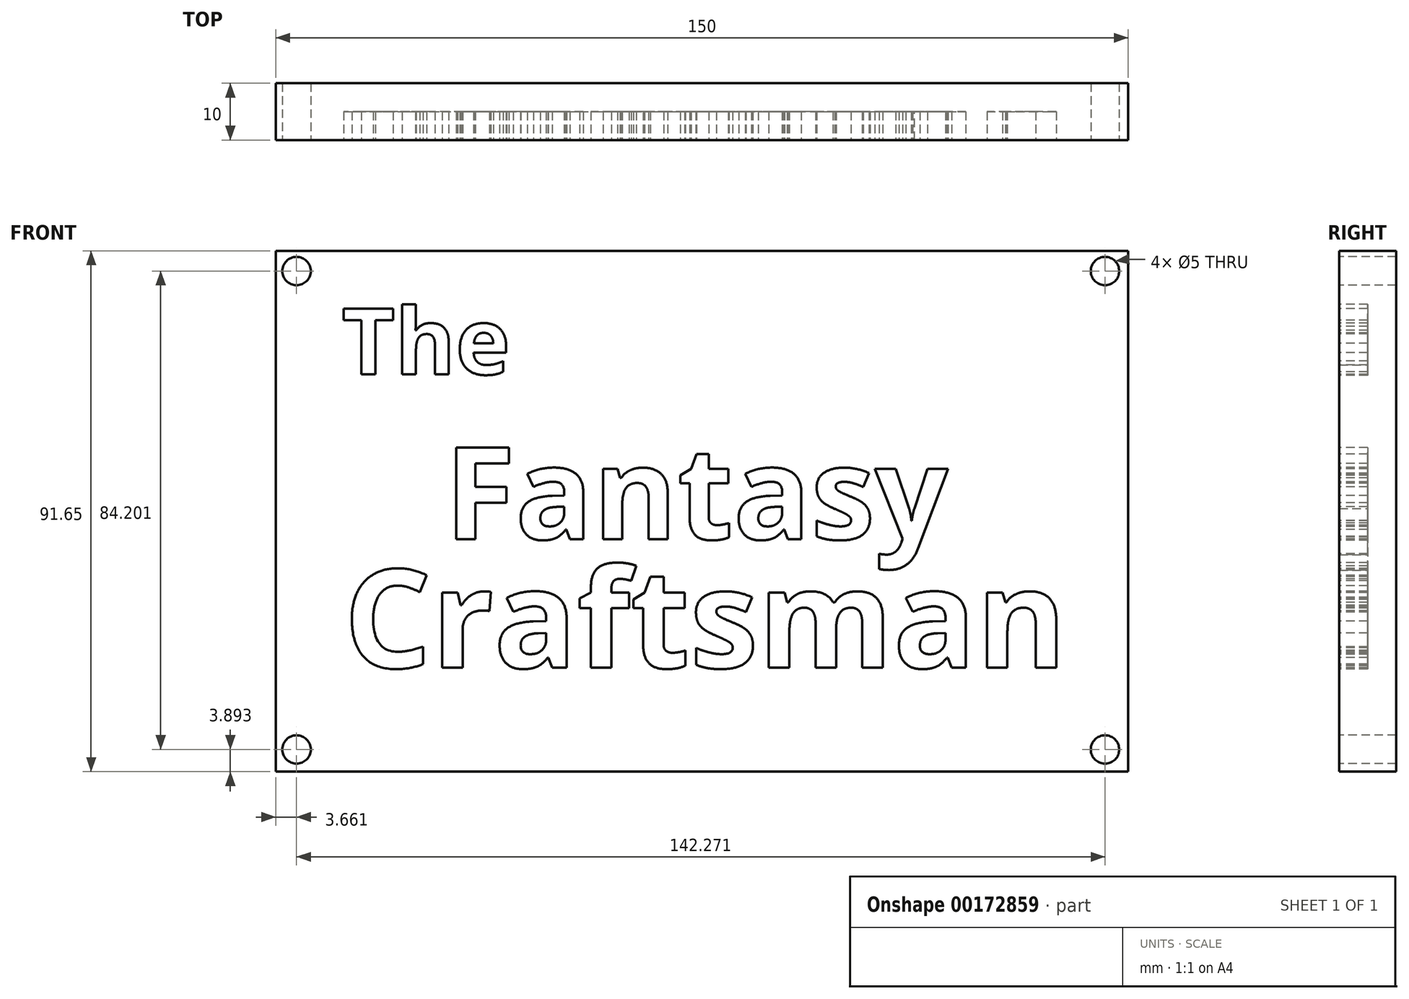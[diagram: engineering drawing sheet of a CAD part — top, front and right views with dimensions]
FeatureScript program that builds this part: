
annotation { "Feature Type Name" : "Feature", "Feature Type Description" : "" }
export const myFeature = defineFeature(function(context is Context, id is Id, definition is map)
    precondition{}
    {
        {
            var Q0;
            Q0=qCreatedBy(makeId("Front.planeOp"),FACE);
            var sketch = newSketch(context, id + "F0", { "sketchPlane" : qUnion([Q0])});
            skLineSegment(sketch, "E0.bottom", {"start": v(-73.96, 55.96) * mm, "end": v(76.04, 55.96) * mm});
            skLineSegment(sketch, "E0.top", {"start": v(-73.96, -35.7) * mm, "end": v(76.04, -35.7) * mm});
            skLineSegment(sketch, "E0.left", {"start": v(-73.96, 55.96) * mm, "end": v(-73.96, -35.7) * mm});
            skLineSegment(sketch, "E0.right", {"start": v(76.04, 55.96) * mm, "end": v(76.04, -35.7) * mm});
            skSolve(sketch);
        }
        {
            var Q0;
            Q0=makeQuery(id+"F0.imprint","IMPRINT",FACE,{"disambiguationData":[TD([[makeQuery(id+"F0.imprint","IMPRINT",EDGE,{"derivedFrom":sQuery(id+"F0.wireOp",EDGE,"E0.bottom")}),-1.0]])]});
            extrude(context, id + "F1", {"entities" : qUnion([Q0]), "depth" : 10 * mm});
        }
        {
            var Q0;
            Q0=makeQuery(id+"F1.opExtrude","CAP_FACE",FACE,{"disambiguationData":[OSD([sQuery(id+"F0.wireOp",EDGE,"E0.bottom"),sQuery(id+"F0.wireOp",EDGE,"E0.top"),sQuery(id+"F0.wireOp",EDGE,"E0.left"),sQuery(id+"F0.wireOp",EDGE,"E0.right")])],"isStart":false});
            var sketch = newSketch(context, id + "F2", { "sketchPlane" : qUnion([Q0])});
            skText(sketch, "E1", { "text": "The", "fontName": "OpenSans-Bold.ttf"});
            const initialGuessF2  = {"E1": [-0.06236, 0.03423, 1, 0, 0.01168]};
            skSetInitialGuess(sketch, initialGuessF2);
            skSolve(sketch);
        }
        {
            var Q0;
            Q0=makeQuery(id+"F2.imprint","IMPRINT",FACE,{"disambiguationData":[TD([[makeQuery(id+"F2.imprint","IMPRINT",EDGE,{"derivedFrom":sQuery(id+"F2.wireOp",EDGE,"E1.sketch_text.stroke-0")}),1.0]])]});
            var sketch = newSketch(context, id + "F3", { "sketchPlane" : qUnion([Q0])});
            skText(sketch, "E2", { "text": "Fantasy", "fontName": "OpenSans-Bold.ttf"});
            const initialGuessF3  = {"E2": [-0.04422, 0.00522, 1, 0, 0.01629]};
            skSetInitialGuess(sketch, initialGuessF3);
            skSolve(sketch);
        }
        {
            var Q0;
            Q0=makeQuery(id+"F2.imprint","IMPRINT",FACE,{"disambiguationData":[TD([[makeQuery(id+"F2.imprint","IMPRINT",EDGE,{"derivedFrom":sQuery(id+"F2.wireOp",EDGE,"E1.sketch_text.stroke-0")}),1.0]])]});
            var sketch = newSketch(context, id + "F4", { "sketchPlane" : qUnion([Q0])});
            skText(sketch, "E3", { "text": "Craftsman", "fontName": "OpenSans-Bold.ttf"});
            const initialGuessF4  = {"E3": [-0.06198, -0.01742, 1, 0, 0.01742]};
            skSetInitialGuess(sketch, initialGuessF4);
            skSolve(sketch);
        }
        {
            var Q0;
            Q0=makeQuery(id+"F2.imprint","IMPRINT",FACE,{"disambiguationData":[TD([[makeQuery(id+"F2.imprint","IMPRINT",EDGE,{"derivedFrom":sQuery(id+"F2.wireOp",EDGE,"E1.sketch_text.stroke-0")}),1.0]])]});
            var sketch = newSketch(context, id + "F5", { "sketchPlane" : qUnion([Q0])});
            skPoint(sketch, "E4", {"position": v(-70.3, 52.4) * mm});
            skPoint(sketch, "E5", {"position": v(-70.3, -31.8) * mm});
            skPoint(sketch, "E6", {"position": v(71.97, -31.8) * mm});
            skPoint(sketch, "E7", {"position": v(71.97, 52.4) * mm});
            skSolve(sketch);
        }
        {
            var Q0;
            Q0=sQuery(id+"F5.wireOp",VERTEX,"E4");
            var Q1;
            Q1=sQuery(id+"F5.wireOp",VERTEX,"E5");
            var Q2;
            Q2=sQuery(id+"F5.wireOp",VERTEX,"E7");
            var Q3;
            Q3=sQuery(id+"F5.wireOp",VERTEX,"E6");
            var Q4;
            Q4=makeQuery(id+"F1.opExtrude","SWEPT_BODY",BODY,{"disambiguationData":[OSD([sQuery(id+"F0.wireOp",EDGE,"E0.bottom"),sQuery(id+"F0.wireOp",EDGE,"E0.top"),sQuery(id+"F0.wireOp",EDGE,"E0.left"),sQuery(id+"F0.wireOp",EDGE,"E0.right")])]});
            hole(context, id + "F6", {"style" : HoleStyle.SIMPLE, "endStyle" : HoleEndStyle.THROUGH, "holeDiameter" : 5 * mm, "locations" : qUnion([Q0, Q1, Q2, Q3]), "scope" : qUnion([Q4]), "isTappedThrough" : true});
        }
        {
            var Q0;
            Q0 = qSketchRegion(id + "F2", true);
            var Q1;
            Q1 = qSketchRegion(id + "F3", true);
            var Q2;
            Q2 = qSketchRegion(id + "F4", true);
            extrude(context, id + "F7", {"entities" : qUnion([Q0, Q1, Q2]), "operationType" : NewBodyOperationType.REMOVE, "oppositeDirection" : true, "depth" : 5 * mm});
        }
    });
